# Revit family: Zumtobel ARTSIGN 75 P MRC
name_source: partatom
category: Lighting Fixtures
revit_build: Autodesk Revit 2016 (Build: 20150220_1215(x64)
units: mm (PartAtom-declared; Revit-internal decimal feet)

## family parameters
Cut with Voids When Loaded = No
Host = Face
Light Source = Yes
OmniClass Number = 23.80.70.11
OmniClass Title = Luminaries for Internal Lighting
Part Type = Normal
Room Calculation Point = No
Round Connector Dimension = Use Diameter
Shared = No

## types (4) — shared parameters
Apparent Load = 2 VA
Assembly Code = D5020200
Body = Zumtobel_Metal_Aluminium
Color Filter = 16777215
Depth = 53 mm  [stored 0.173885 ft]
Description = Escape sign LED luminaire ceiling-recessed
Dimming Lamp Color Temperature Shift = <None>
Emit Shape Visible in Rendering = No
Emit from Rectangle Length = 155 mm  [stored 0.50853 ft]
Emit from Rectangle Width = 305 mm  [stored 1.00066 ft]
Height = 184 mm  [stored 0.603675 ft]
Lamp = LED
Manufacturer = Zumtobel Lighting
Photometric Web File = 42185911_(STD_LEO).IES
Tilt Angle = 180.00°
URL = http://www.zumtobel.com
Voltage = 230 V
Width = 188 mm  [stored 0.616798 ft]
zero-valued in all types: Default Elevation

## per-type parameters (varying)
| type | Escape Down | Escape Left | Escape Right | Escape Up | Model |
| ARTSIGN 75 P MRC ECD SR SP-1D | Yes | No | No | No | 42185911+22166895 |
| ARTSIGN 75 P MRC ECD SR SP-1L | No | Yes | No | No | 42185911+22166893 |
| ARTSIGN 75 P MRC ECD SR SP-1R | No | No | Yes | No | 42185911+22166894 |
| ARTSIGN 75 P MRC ECD SR SP-1UP | No | No | No | Yes | 42185911+22900379 |

note: [stored X ft] marks values corroborated as IEEE doubles in the binary element streams (Revit-internal decimal feet)

## geometry (parser evidence)
native form markers: Sweep x2
no freeform markers — native parametric forms only
